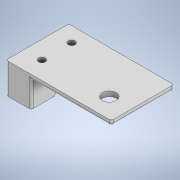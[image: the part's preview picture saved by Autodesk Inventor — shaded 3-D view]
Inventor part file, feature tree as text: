
AUTODESK INVENTOR PART (.ipt)
format: ipt  version: 2022.3 (Build 263350000, 350)  size: 174,080 bytes
history: native  units: in
note: dims shown in document units (in); Inventor stores cm internally (conversion verified against a paired STEP export)
features: extrude x7, sketch x7, fillet x1
ambient origin geometry x8: Origin, YZ Plane, XZ Plane, XY Plane, X Axis, Y Axis, Z Axis, Center Point
bodies: Solid1 (feature_tree)
feature tree (15):
  extrude  "Extrusion1"  Depth=2.65in
  extrude  "Extrusion2"  Depth=0.125in
  extrude  "Extrusion3"  Depth=0.25in TaperAngle=0.0deg
  extrude  "Extrusion4"  Depth=0.65in TaperAngle=0.0deg
  extrude  "Extrusion5"  Depth=0.25in TaperAngle=0.0deg
  extrude  "Extrusion6"  Depth=0.25in
  fillet  "Fillet1"  Radius=0.375in
  extrude  "Extrusion7"  Depth=0.375in
  sketch  "Sketch1"  dims[d0=1.575in d1=2.65in]
  sketch  "Sketch2"  dims[d2=0.125in d3=0.0in d4=0.55in]
  sketch  "Sketch3"  dims[d5=0.5in d6=0.25in d7=0.0in]
  sketch  "Sketch4"  dims[d8=0.625in d9=0.65in d10=0.0in]
  sketch  "Sketch5"  dims[d11=0.5in d12=0.25in d13=0.0in]
  sketch  "Sketch6"  dims[d14=0.63in d15=0.25in d16=0.375in]
  sketch  "Sketch7"  dims[d17=0.1in d18=0.0in d19=0.1719in d20=0.1719in d21=0.45in d22=0.45in d23=0.75in d25=1.0in d26=0.0in d27=0.05in d28=0.35in d29=0.375in d30=1.0in d31=0.0in d32=0.375in]
